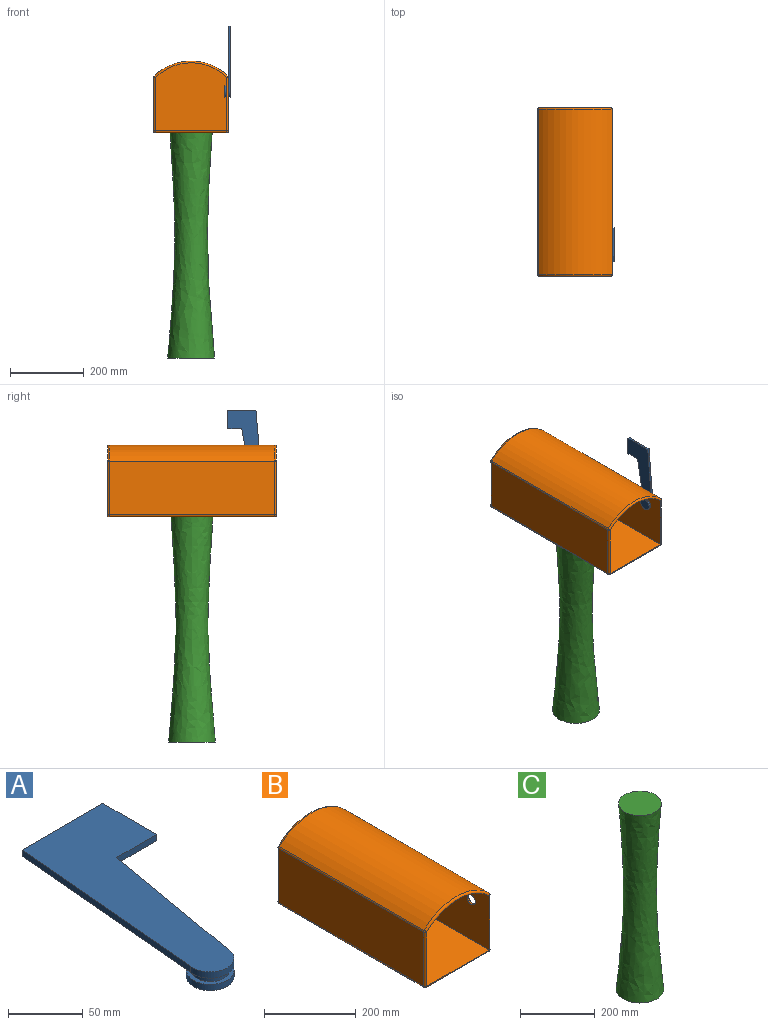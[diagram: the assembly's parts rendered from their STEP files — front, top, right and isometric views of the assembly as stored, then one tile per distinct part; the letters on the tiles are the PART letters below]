
ASSEMBLY  parts=3 mates=2
PART A: 12 faces, bbox 91.7x193x15.2 mm
  f0: cylinder r=15.88mm len=31.75mm, axis (0,0,-1), area 506.7mm2, adj f1,f2
  f1: plane 31.75x31.75mm, normal (0,0,1), area 285mm2, adj f0,f3
  f2: plane 31.75x31.75mm, normal (0,0,-1), area 791.7mm2, adj f0
  f3: cylinder r=12.7mm len=25.4mm, axis (0,0,-1), area 405.4mm2, adj f1,f11
  f4: plane 174.37x15.26mm, normal (-1,0.09,0), area 889.2mm2, adj f5,f9,f10,f11
  f5: cylinder r=15.88mm len=31.75mm, axis (0,0,-1), area 267.4mm2, adj f4,f6,f10,f11
  f6: plane 126.32x22.27mm, normal (0.98,-0.17,0), area 651.6mm2, adj f5,f7,f10,f11
  f7: plane 37.67x5.08mm, normal (0,-1,0), area 191.4mm2, adj f6,f8,f10,f11
  f8: plane 50.8x5.08mm, normal (1,0,0), area 258.1mm2, adj f7,f9,f10,f11
  f9: plane 76.2x5.08mm, normal (0,1,0), area 387.1mm2, adj f4,f8,f10,f11
  f10: plane 193x91.7mm, normal (0,0,1), area 9099.4mm2, adj f4,f5,f6,f7,f8,f9
  f11: plane 193x91.7mm, normal (0,0,-1), area 8592.7mm2, adj f3,f4,f5,f6,f7,f8,f9
PART B: 31 faces, bbox 216.6x457.2x206.3 mm
  f0: plane 193.04x184.32mm, normal (0,1,0), area 33225.9mm2, adj f10,f13,f17,f18
  f1: plane 447.04x193.04mm, normal (0,0,-1), area 86296.6mm2, adj f16,f17,f25,f26
  f2: plane 447.04x145.19mm, normal (1,0,0), area 64400.6mm2, adj f10,f14,f15,f16,f30
  f3: cylinder r=143.68mm len=447.04mm, axis (0,-1,0), area 98960.5mm2, adj f13,f14,f23,f24
  f4: plane 447.04x145.19mm, normal (-1,0,0), area 64907.3mm2, adj f18,f23,f26,f29
  f5: plane 193.04x184.32mm, normal (0,-1,0), area 33225.9mm2, adj f6,f7,f8,f9
  f6: plane 452.12x193.04mm, normal (0,0,1), area 87277.2mm2, adj f5,f7,f9,f25
  f7: plane 452.12x145.19mm, normal (-1,0,0), area 65138.2mm2, adj f5,f6,f8,f15,f30
  f8: cylinder r=138.6mm len=452.12mm, axis (0,-1,0), area 96546.5mm2, adj f5,f7,f9,f24
  f9: plane 452.12x145.19mm, normal (1,0,0), area 65644.9mm2, adj f5,f6,f8,f29
  f10: cylinder r=5.08mm len=145.19mm, axis (0,0,-1), area 1158.6mm2, adj f0,f2,f11,f12
  f11: sphere r=5.08mm, area 20.7mm2, adj f10,f13,f14
  f12: sphere r=5.08mm, area 40.5mm2, adj f10,f16,f17
  f13: torus R=138.6mm, axis (0,-1,0), area 1743.7mm2, adj f0,f3,f11,f19
  f14: cylinder r=5.08mm len=447.04mm, axis (0,-1,0), area 1817.8mm2, adj f2,f3,f11,f20
  f15: cylinder r=5.08mm len=145.19mm, axis (0,0,1), area 1158.6mm2, adj f2,f7,f20,f21
  f16: cylinder r=5.08mm len=447.04mm, axis (0,-1,0), area 3567.2mm2, adj f1,f2,f12,f21
  f17: cylinder r=5.08mm len=193.04mm, axis (-1,0,0), area 1540.4mm2, adj f0,f1,f12,f22
  f18: cylinder r=5.08mm len=145.19mm, axis (0,0,-1), area 1158.6mm2, adj f0,f4,f19,f22
  f19: sphere r=5.08mm, area 20.7mm2, adj f13,f18,f23
  f20: sphere r=5.08mm, area 20.7mm2, adj f14,f15,f24
  f21: sphere r=5.08mm, area 40.5mm2, adj f15,f16,f25
  f22: sphere r=5.08mm, area 40.5mm2, adj f17,f18,f26
  f23: cylinder r=5.08mm len=447.04mm, axis (0,-1,0), area 1817.8mm2, adj f3,f4,f19,f27
  f24: torus R=138.6mm, axis (0,-1,0), area 1743.7mm2, adj f3,f8,f20,f27
  f25: cylinder r=5.08mm len=193.04mm, axis (1,0,0), area 1540.4mm2, adj f1,f6,f21,f28
  f26: cylinder r=5.08mm len=447.04mm, axis (0,1,0), area 3567.2mm2, adj f1,f4,f22,f28
  f27: sphere r=5.08mm, area 20.7mm2, adj f23,f24,f29
  f28: sphere r=5.08mm, area 40.5mm2, adj f25,f26,f29
  f29: cylinder r=5.08mm len=145.19mm, axis (0,0,1), area 1158.6mm2, adj f4,f9,f27,f28
  f30: cylinder r=12.7mm len=25.4mm, axis (1,0,0), area 405.4mm2, adj f2,f7
PART C: 3 faces, bbox 127x127x609.6 mm
  f0: plane 127x127mm, normal (0,0,-1), area 12666.8mm2, adj f2
  f1: plane 114.3x114.3mm, normal (0,0,1), area 10260.1mm2, adj f2
  f2: bspline ~609.6x127mm, area 193402.8mm2, adj f0,f1
PLACE A rot(axis=(0.58,0.58,0.58),120deg) t=(-196.42,-268.57,508.23)mm
PLACE B t=(-287.86,132.75,396.06)mm
PLACE C t=(-287.86,-95.85,-213.54)mm fixed
MATE fastened B.f1 <-> C.f1  axis (0,0,-1) through (-287.86,-95.85,396.06)mm
MATE revolute A.f3 <-> B.f30  axis (1,0,0) through (-191.34,-268.57,508.23)mm
